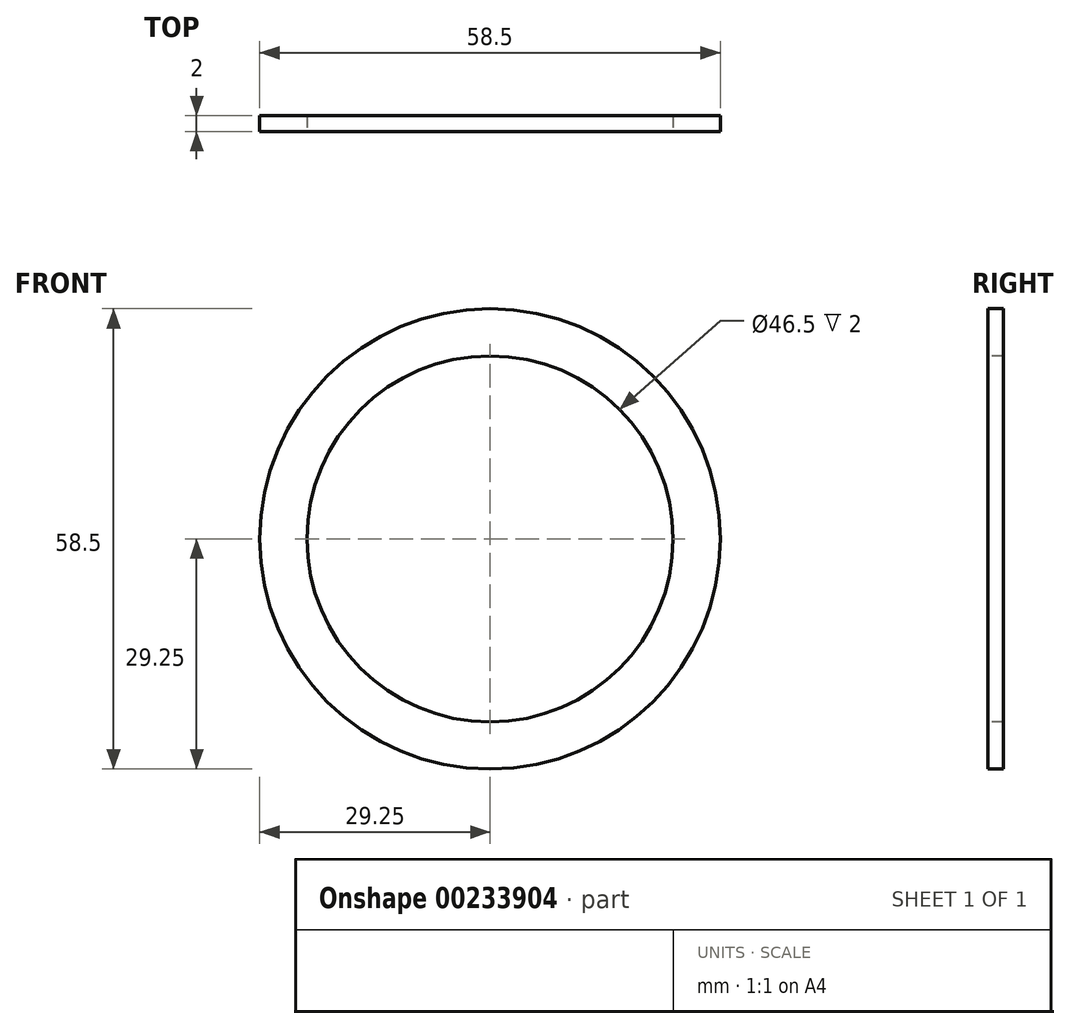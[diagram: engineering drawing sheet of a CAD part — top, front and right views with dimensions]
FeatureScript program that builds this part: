
annotation { "Feature Type Name" : "Feature", "Feature Type Description" : "" }
export const myFeature = defineFeature(function(context is Context, id is Id, definition is map)
    precondition{}
    {
        {
            var Q0;
            Q0=qCreatedBy(makeId("Top.planeOp"),FACE);
            var sketch = newSketch(context, id + "F0", { "sketchPlane" : qUnion([Q0])});
            skLineSegment(sketch, "E0", {"start": v(0, -54.93) * mm, "end": v(0, 83.95) * mm, "construction": true});
            skLineSegment(sketch, "E1", {"start": v(29.25, -27.69) * mm, "end": v(29.25, 27.24) * mm, "construction": true});
            skLineSegment(sketch, "E2.bottom", {"start": v(29.25, 0) * mm, "end": v(23.25, 0) * mm});
            skLineSegment(sketch, "E2.top", {"start": v(29.25, -2) * mm, "end": v(23.25, -2) * mm});
            skLineSegment(sketch, "E2.left", {"start": v(29.25, 0) * mm, "end": v(29.25, -2) * mm});
            skLineSegment(sketch, "E2.right", {"start": v(23.25, 0) * mm, "end": v(23.25, -2) * mm});
            skSolve(sketch);
        }
        {
            var Q0;
            Q0=makeQuery(id+"F0.imprint","IMPRINT",FACE,{"disambiguationData":[TD([[makeQuery(id+"F0.imprint","IMPRINT",EDGE,{"derivedFrom":sQuery(id+"F0.wireOp",EDGE,"E2.bottom")}),1.0]])]});
            var Q1;
            Q1=sQuery(id+"F0.wireOp",EDGE,"E0");
            revolve(context, id + "F1", {"entities" : qUnion([Q0]), "axis" : qUnion([Q1]), "revolveType" : RevolveType.FULL});
        }
    });
